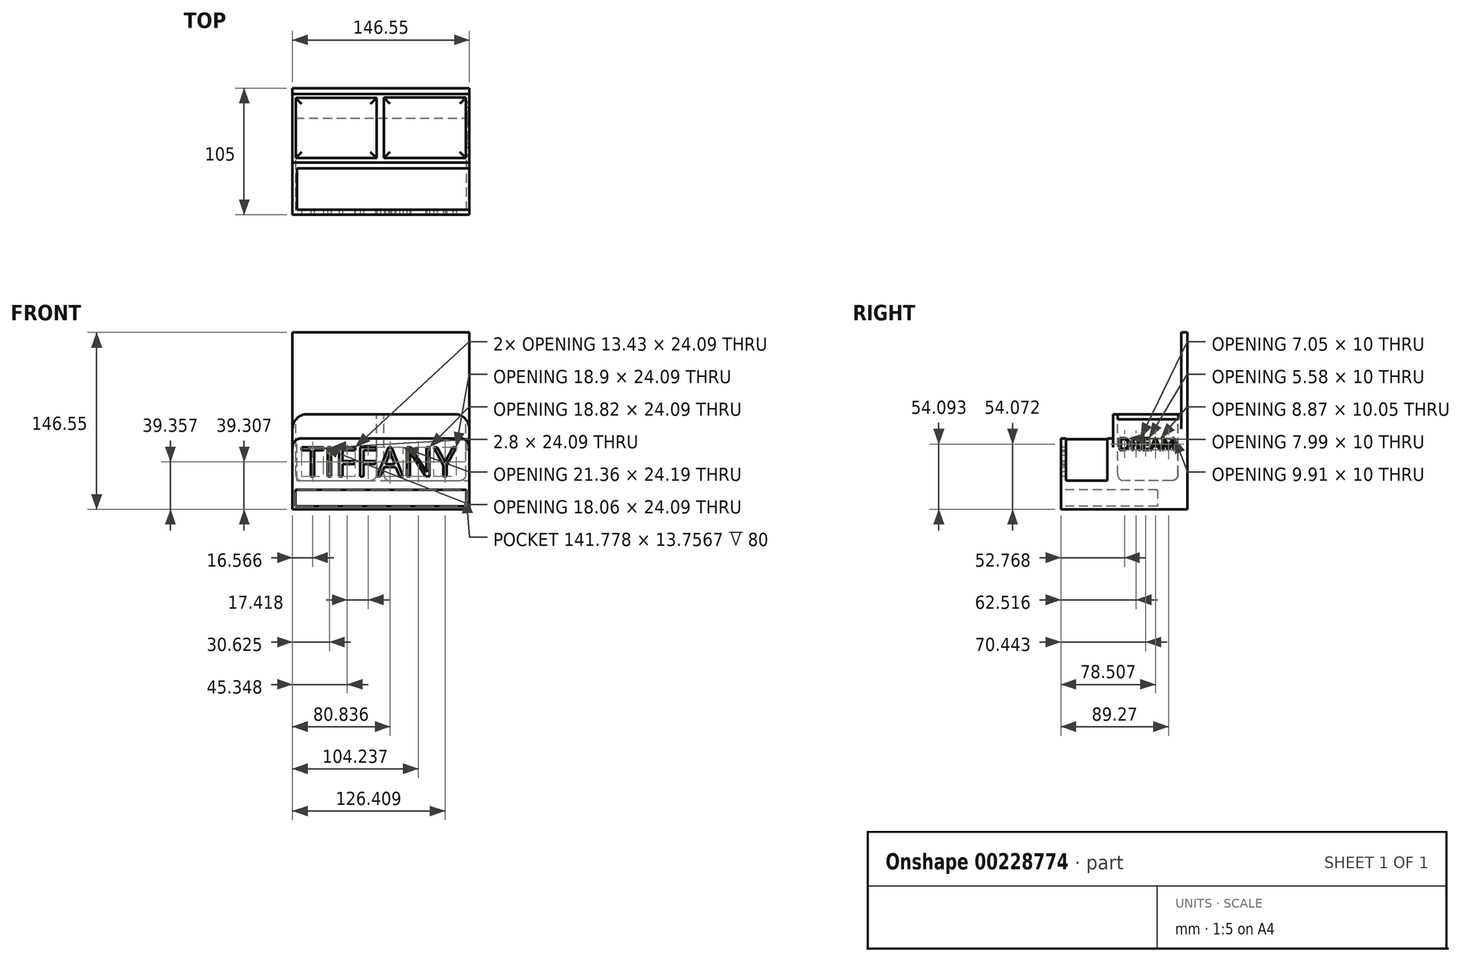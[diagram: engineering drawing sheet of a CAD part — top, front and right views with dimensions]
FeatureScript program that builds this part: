
annotation { "Feature Type Name" : "Feature", "Feature Type Description" : "" }
export const myFeature = defineFeature(function(context is Context, id is Id, definition is map)
    precondition{}
    {
        {
            var Q0;
            Q0=qCreatedBy(makeId("Front.planeOp"),FACE);
            var sketch = newSketch(context, id + "F0", { "sketchPlane" : qUnion([Q0])});
            skLineSegment(sketch, "E0.bottom", {"start": v(-73, 72.85) * mm, "end": v(73.56, 72.85) * mm});
            skLineSegment(sketch, "E0.top", {"start": v(-73, -73.7) * mm, "end": v(73.56, -73.7) * mm});
            skLineSegment(sketch, "E0.left", {"start": v(-73, 72.85) * mm, "end": v(-73, -73.7) * mm});
            skLineSegment(sketch, "E0.right", {"start": v(73.56, 72.85) * mm, "end": v(73.56, -73.7) * mm});
            skSolve(sketch);
        }
        {
            var Q0;
            Q0 = qSketchRegion(id + "F0", true);
            var Q1;
            Q1 = qSketchRegion(id + "F2", true);
            extrude(context, id + "F1", {"entities" : qUnion([Q0, Q1]), "depth" : 5 * mm});
        }
        {
            var Q0;
            Q0=makeQuery(id+"F1.opExtrude","CAP_FACE",FACE,{"disambiguationData":[OSD([sQuery(id+"F0.wireOp",EDGE,"E0.bottom"),sQuery(id+"F0.wireOp",EDGE,"E0.top"),sQuery(id+"F0.wireOp",EDGE,"E0.left"),sQuery(id+"F0.wireOp",EDGE,"E0.right")])],"isStart":false});
            var sketch = newSketch(context, id + "F2", { "sketchPlane" : qUnion([Q0])});
            skLineSegment(sketch, "E1.bottom", {"start": v(-73, -54.89) * mm, "end": v(73.56, -54.89) * mm});
            skLineSegment(sketch, "E1.top", {"start": v(-73, -73.7) * mm, "end": v(73.56, -73.7) * mm});
            skLineSegment(sketch, "E1.left", {"start": v(-73, -54.89) * mm, "end": v(-73, -73.7) * mm});
            skLineSegment(sketch, "E1.right", {"start": v(73.56, -54.89) * mm, "end": v(73.56, -73.7) * mm});
            skSolve(sketch);
        }
        {
            var Q0;
            Q0=makeQuery(id+"F2.imprint","IMPRINT",FACE,{"disambiguationData":[TD([[makeQuery(id+"F2.imprint","IMPRINT",EDGE,{"derivedFrom":sQuery(id+"F2.wireOp",EDGE,"E1.bottom")}),-1.0]])]});
            extrude(context, id + "F3", {"entities" : qUnion([Q0]), "operationType" : NewBodyOperationType.ADD, "depth" : 100 * mm});
        }
        {
            var Q0;
            Q0=makeQuery(id+"F3.opExtrude","CAP_FACE",FACE,{"disambiguationData":[OSD([sQuery(id+"F2.wireOp",EDGE,"E1.bottom"),sQuery(id+"F2.wireOp",EDGE,"E1.top"),sQuery(id+"F2.wireOp",EDGE,"E1.left"),sQuery(id+"F2.wireOp",EDGE,"E1.right")])],"isStart":false});
            var sketch = newSketch(context, id + "F4", { "sketchPlane" : qUnion([Q0])});
            skLineSegment(sketch, "E2.bottom", {"start": v(-70.75, -57.41) * mm, "end": v(71.03, -57.41) * mm});
            skLineSegment(sketch, "E2.top", {"start": v(-70.75, -71.17) * mm, "end": v(71.03, -71.17) * mm});
            skLineSegment(sketch, "E2.left", {"start": v(-70.75, -57.41) * mm, "end": v(-70.75, -71.17) * mm});
            skLineSegment(sketch, "E2.right", {"start": v(71.03, -57.41) * mm, "end": v(71.03, -71.17) * mm});
            skSolve(sketch);
        }
        {
            var Q0;
            Q0 = qSketchRegion(id + "F4", true);
            extrude(context, id + "F5", {"entities" : qUnion([Q0]), "operationType" : NewBodyOperationType.REMOVE, "oppositeDirection" : true, "depth" : 80 * mm});
        }
        {
            var Q0;
            Q0=makeQuery(id+"F3.opExtrude","SWEPT_FACE",FACE,{"disambiguationData":[OSD([sQuery(id+"F2.wireOp",EDGE,"E1.bottom")])]});
            var sketch = newSketch(context, id + "F6", { "sketchPlane" : qUnion([Q0])});
            skLineSegment(sketch, "E3.bottom", {"start": v(-73, -5) * mm, "end": v(0, -5) * mm});
            skLineSegment(sketch, "E3.top", {"start": v(-73, -61.66) * mm, "end": v(0, -61.66) * mm});
            skLineSegment(sketch, "E3.left", {"start": v(-73, -5) * mm, "end": v(-73, -61.66) * mm});
            skLineSegment(sketch, "E3.right", {"start": v(0, -5) * mm, "end": v(0, -61.66) * mm});
            skLineSegment(sketch, "E4.bottom", {"start": v(0, -5) * mm, "end": v(73.56, -5) * mm});
            skLineSegment(sketch, "E4.top", {"start": v(0, -61.66) * mm, "end": v(73.56, -61.66) * mm});
            skLineSegment(sketch, "E4.right", {"start": v(73.56, -5) * mm, "end": v(73.56, -61.66) * mm});
            skSolve(sketch);
        }
        {
            var Q0;
            Q0 = qSketchRegion(id + "F6", true);
            extrude(context, id + "F7", {"entities" : qUnion([Q0]), "operationType" : NewBodyOperationType.ADD, "depth" : 60 * mm});
        }
        {
            var Q0;
            Q0=makeQuery(id+"F7.opExtrude","CAP_FACE",FACE,{"disambiguationData":[OSD([sQuery(id+"F6.wireOp",EDGE,"E3.bottom"),sQuery(id+"F6.wireOp",EDGE,"E3.top"),sQuery(id+"F6.wireOp",EDGE,"E3.left"),sQuery(id+"F6.wireOp",EDGE,"E4.bottom"),sQuery(id+"F6.wireOp",EDGE,"E4.top"),sQuery(id+"F6.wireOp",EDGE,"E4.right")])],"isStart":false});
            var sketch = newSketch(context, id + "F8", { "sketchPlane" : qUnion([Q0])});
            skLineSegment(sketch, "E5.bottom", {"start": v(-70.41, -8.1) * mm, "end": v(-3.37, -8.1) * mm});
            skLineSegment(sketch, "E5.top", {"start": v(-70.41, -57.95) * mm, "end": v(-3.37, -57.95) * mm});
            skLineSegment(sketch, "E5.left", {"start": v(-70.41, -8.1) * mm, "end": v(-70.41, -57.95) * mm});
            skLineSegment(sketch, "E5.right", {"start": v(-3.37, -8.1) * mm, "end": v(-3.37, -57.95) * mm});
            skLineSegment(sketch, "E6.bottom", {"start": v(2.7, -7.76) * mm, "end": v(70.75, -7.76) * mm});
            skLineSegment(sketch, "E6.top", {"start": v(2.7, -57.95) * mm, "end": v(70.75, -57.95) * mm});
            skLineSegment(sketch, "E6.left", {"start": v(2.7, -7.76) * mm, "end": v(2.7, -57.95) * mm});
            skLineSegment(sketch, "E6.right", {"start": v(70.75, -7.76) * mm, "end": v(70.75, -57.95) * mm});
            skSolve(sketch);
        }
        {
            var Q0;
            Q0 = qSketchRegion(id + "F8", true);
            extrude(context, id + "F9", {"entities" : qUnion([Q0]), "operationType" : NewBodyOperationType.REMOVE, "oppositeDirection" : true, "depth" : 55 * mm});
        }
        {
            var Q0;
            Q0=makeQuery(id+"F3.opExtrude","SWEPT_FACE",FACE,{"disambiguationData":[OSD([sQuery(id+"F2.wireOp",EDGE,"E1.bottom")])]});
            var sketch = newSketch(context, id + "F10", { "sketchPlane" : qUnion([Q0])});
            skLineSegment(sketch, "E7.bottom", {"start": v(-73, -61.66) * mm, "end": v(73.56, -61.66) * mm});
            skLineSegment(sketch, "E7.top", {"start": v(-73, -105) * mm, "end": v(73.56, -105) * mm});
            skLineSegment(sketch, "E7.left", {"start": v(-73, -61.66) * mm, "end": v(-73, -105) * mm});
            skLineSegment(sketch, "E7.right", {"start": v(73.56, -61.66) * mm, "end": v(73.56, -105) * mm});
            skSolve(sketch);
        }
        {
            var Q0;
            Q0 = qSketchRegion(id + "F10", true);
            extrude(context, id + "F11", {"entities" : qUnion([Q0]), "operationType" : NewBodyOperationType.ADD, "depth" : 40 * mm});
        }
        {
            var Q0;
            Q0=makeQuery(id+"F11.opExtrude","CAP_FACE",FACE,{"disambiguationData":[OSD([sQuery(id+"F10.wireOp",EDGE,"E7.bottom"),sQuery(id+"F10.wireOp",EDGE,"E7.top"),sQuery(id+"F10.wireOp",EDGE,"E7.left"),sQuery(id+"F10.wireOp",EDGE,"E7.right")])],"isStart":false});
            var sketch = newSketch(context, id + "F12", { "sketchPlane" : qUnion([Q0])});
            skLineSegment(sketch, "E8.bottom", {"start": v(-69.17, -66.46) * mm, "end": v(73.56, -66.46) * mm});
            skLineSegment(sketch, "E8.top", {"start": v(-69.17, -100.68) * mm, "end": v(73.56, -100.68) * mm});
            skLineSegment(sketch, "E8.left", {"start": v(-69.17, -66.46) * mm, "end": v(-69.17, -100.68) * mm});
            skLineSegment(sketch, "E8.right", {"start": v(73.56, -66.46) * mm, "end": v(73.56, -100.68) * mm});
            skSolve(sketch);
        }
        {
            var Q0;
            Q0 = qSketchRegion(id + "F12", true);
            extrude(context, id + "F13", {"entities" : qUnion([Q0]), "operationType" : NewBodyOperationType.REMOVE, "oppositeDirection" : true, "depth" : 35 * mm});
        }
        {
            var Q0;
            Q0=makeQuery(id+"F9.boolean.opBoolean","COPY",EDGE,{"derivedFrom":makeQuery(id+"F9.opExtrude","CAP_EDGE",EDGE,{"disambiguationData":[OSD([sQuery(id+"F8.wireOp",EDGE,"E5.bottom")])],"isStart":false})});
            var Q1;
            Q1=makeQuery(id+"F9.boolean.opBoolean","COPY",EDGE,{"derivedFrom":makeQuery(id+"F9.opExtrude","CAP_EDGE",EDGE,{"disambiguationData":[OSD([sQuery(id+"F8.wireOp",EDGE,"E5.left")])],"isStart":false})});
            var Q2;
            Q2=makeQuery(id+"F9.boolean.opBoolean","COPY",FACE,{"derivedFrom":makeQuery(id+"F9.opExtrude","CAP_FACE",FACE,{"disambiguationData":[OSD([sQuery(id+"F8.wireOp",EDGE,"E5.bottom"),sQuery(id+"F8.wireOp",EDGE,"E5.top"),sQuery(id+"F8.wireOp",EDGE,"E5.left"),sQuery(id+"F8.wireOp",EDGE,"E5.right")])],"isStart":false})});
            fillet(context, id + "F14", {"entities" : qUnion([Q0, Q1, Q2]), "radius" : 5 * mm, "tangentPropagation" : true, "allowEdgeOverflow" : false});
        }
        {
            var Q0;
            Q0=makeQuery(id+"F9.boolean.opBoolean","COPY",FACE,{"derivedFrom":makeQuery(id+"F9.opExtrude","CAP_FACE",FACE,{"disambiguationData":[OSD([sQuery(id+"F8.wireOp",EDGE,"E6.bottom"),sQuery(id+"F8.wireOp",EDGE,"E6.top"),sQuery(id+"F8.wireOp",EDGE,"E6.left"),sQuery(id+"F8.wireOp",EDGE,"E6.right")])],"isStart":false})});
            fillet(context, id + "F15", {"entities" : qUnion([Q0]), "radius" : 5 * mm, "tangentPropagation" : true, "allowEdgeOverflow" : false});
        }
        {
            var Q0;
            {var subQ1=sQuery(id+"F10.wireOp",EDGE,"E7.right");var subQ2=sQuery(id+"F10.wireOp",EDGE,"E7.top");Q0=makeQuery(id+"F13.boolean.opBoolean","SPLIT",EDGE,{"disambiguationData":[TD([makeQuery(id+"F11.opExtrude","SWEPT_FACE",FACE,{"disambiguationData":[OSD([subQ2])]})])],"derivedFrom":makeQuery(id+"F11.opExtrude","CAP_EDGE",EDGE,{"disambiguationData":[OSD([subQ1])],"isStart":false})});}
            var Q1;
            {var subQ0=sQuery(id+"F10.wireOp",EDGE,"E7.right");Q1=makeQuery(id+"F13.boolean.opBoolean","SPLIT",EDGE,{"disambiguationData":[TD([makeQuery(id+"F13.opExtrude","SWEPT_FACE",FACE,{"disambiguationData":[OSD([sQuery(id+"F12.wireOp",EDGE,"E8.bottom")])]})])],"derivedFrom":makeQuery(id+"F11.opExtrude","CAP_EDGE",EDGE,{"disambiguationData":[OSD([subQ0])],"isStart":false})});}
            var Q2;
            Q2=makeQuery(id+"F11.opExtrude","CAP_EDGE",EDGE,{"disambiguationData":[OSD([sQuery(id+"F10.wireOp",EDGE,"E7.left")])],"isStart":false});
            fillet(context, id + "F16", {"entities" : qUnion([Q0, Q1, Q2]), "radius" : 7.24 * mm, "tangentPropagation" : true, "allowEdgeOverflow" : false});
        }
        {
            var Q0;
            Q0=makeQuery(id+"F7.opExtrude","CAP_EDGE",EDGE,{"disambiguationData":[OSD([sQuery(id+"F6.wireOp",EDGE,"E3.left")])],"isStart":false});
            var Q1;
            Q1=makeQuery(id+"F7.opExtrude","CAP_EDGE",EDGE,{"disambiguationData":[OSD([sQuery(id+"F6.wireOp",EDGE,"E4.right")])],"isStart":false});
            fillet(context, id + "F17", {"entities" : qUnion([Q0, Q1]), "radius" : 12.07 * mm, "tangentPropagation" : true, "allowEdgeOverflow" : false});
        }
        {
            var Q0;
            Q0=makeQuery(id+"F11.boolean.opBoolean","MERGE",FACE,{"derivedFrom":[makeQuery(id+"F7.boolean.opBoolean","MERGE",FACE,{"derivedFrom":[makeQuery(id+"F3.boolean.opBoolean","MERGE",FACE,{"derivedFrom":[makeQuery(id+"F1.opExtrude","SWEPT_FACE",FACE,{"disambiguationData":[OSD([sQuery(id+"F0.wireOp",EDGE,"E0.right")])]}),makeQuery(id+"F3.opExtrude","SWEPT_FACE",FACE,{"disambiguationData":[OSD([sQuery(id+"F2.wireOp",EDGE,"E1.right")])]})]}),makeQuery(id+"F7.opExtrude","SWEPT_FACE",FACE,{"disambiguationData":[OSD([sQuery(id+"F6.wireOp",EDGE,"E4.right")])]})]}),makeQuery(id+"F11.opExtrude","SWEPT_FACE",FACE,{"disambiguationData":[OSD([sQuery(id+"F10.wireOp",EDGE,"E7.right")])]})]});
            var sketch = newSketch(context, id + "F18", { "sketchPlane" : qUnion([Q0])});
            skText(sketch, "E9", { "text": "DREAM", "fontName": "OpenSans-Regular.ttf"});
            skPoint(sketch, "E9.firstSnap0", {"position": v(-61.66, -14.55) * mm});
            const initialGuessF18  = {"E9": [-0.0576, -0.02463, 1, 0, 0.01009]};
            skSetInitialGuess(sketch, initialGuessF18);
            skSolve(sketch);
        }
        {
            var Q0;
            Q0 = qSketchRegion(id + "F18", true);
            extrude(context, id + "F19", {"entities" : qUnion([Q0]), "operationType" : NewBodyOperationType.REMOVE, "oppositeDirection" : true, "depth" : 5 * mm});
        }
        {
            var Q0;
            Q0=makeQuery(id+"F11.boolean.opBoolean","MERGE",FACE,{"derivedFrom":[makeQuery(id+"F3.opExtrude","CAP_FACE",FACE,{"disambiguationData":[OSD([sQuery(id+"F2.wireOp",EDGE,"E1.bottom"),sQuery(id+"F2.wireOp",EDGE,"E1.top"),sQuery(id+"F2.wireOp",EDGE,"E1.left"),sQuery(id+"F2.wireOp",EDGE,"E1.right")])],"isStart":false}),makeQuery(id+"F11.opExtrude","SWEPT_FACE",FACE,{"disambiguationData":[OSD([sQuery(id+"F10.wireOp",EDGE,"E7.top")])]})]});
            var sketch = newSketch(context, id + "F20", { "sketchPlane" : qUnion([Q0])});
            skText(sketch, "E10", { "text": "TIFFANY", "fontName": "OpenSans-Regular.ttf"});
            const initialGuessF20  = {"E10": [-0.06575, -0.04644, 1, 0, 0.0243]};
            skSetInitialGuess(sketch, initialGuessF20);
            skSolve(sketch);
        }
        {
            var Q0;
            Q0 = qSketchRegion(id + "F20", true);
            extrude(context, id + "F21", {"entities" : qUnion([Q0]), "operationType" : NewBodyOperationType.REMOVE, "oppositeDirection" : true, "depth" : 5 * mm});
        }
    });
